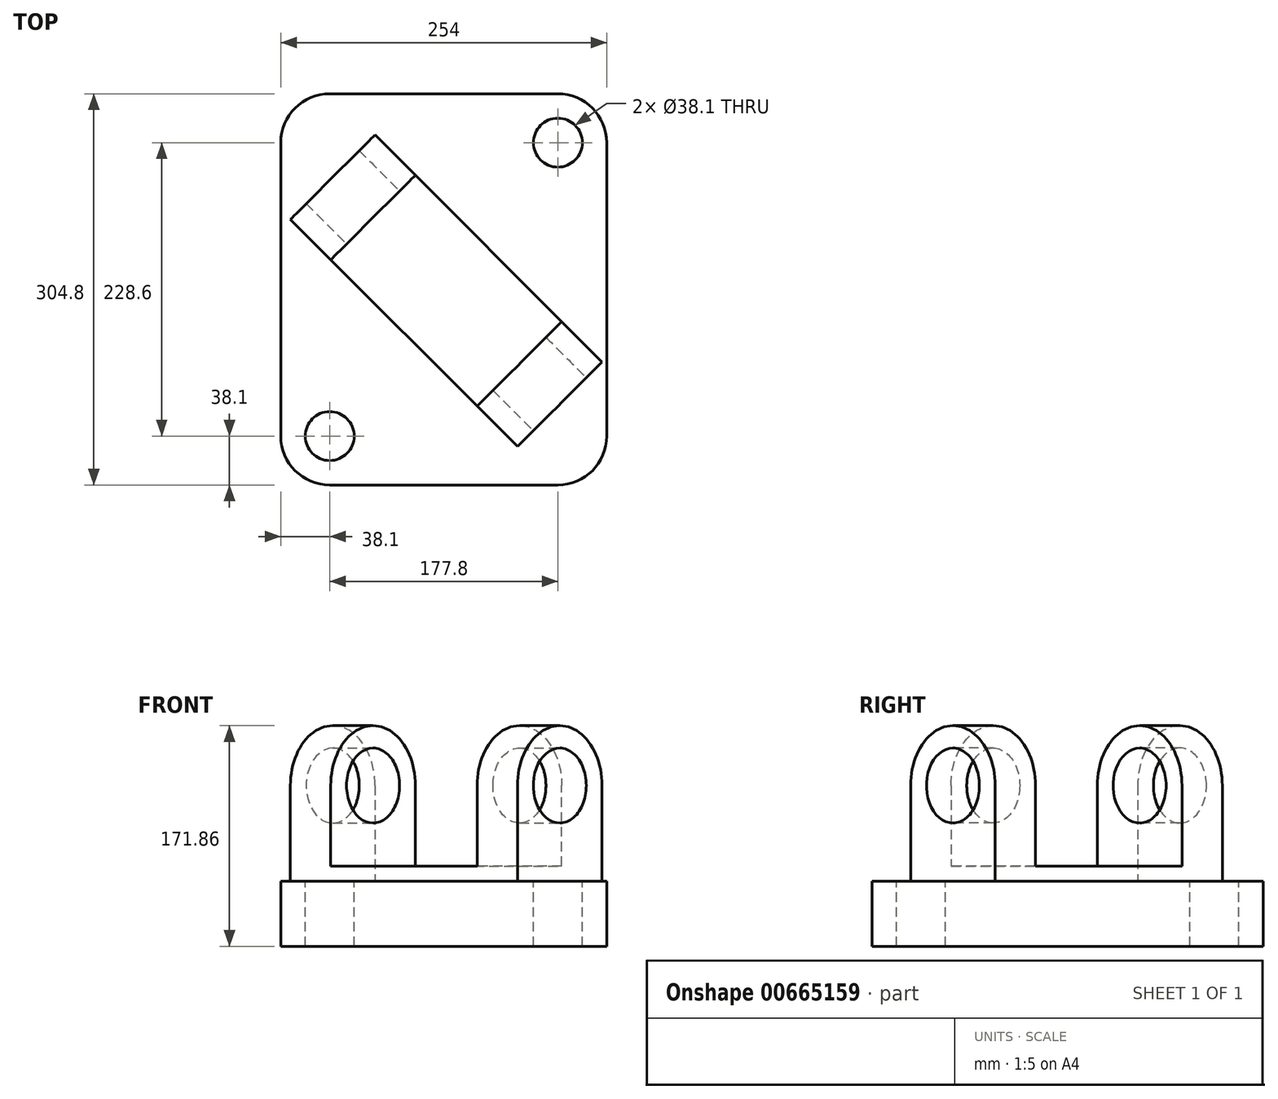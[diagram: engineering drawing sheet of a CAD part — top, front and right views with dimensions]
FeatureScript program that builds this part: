
annotation { "Feature Type Name" : "Feature", "Feature Type Description" : "" }
export const myFeature = defineFeature(function(context is Context, id is Id, definition is map)
    precondition{}
    {
        {
            var Q0;
            Q0=qCreatedBy(makeId("Top.planeOp"),FACE);
            var sketch = newSketch(context, id + "F0", { "sketchPlane" : qUnion([Q0])});
            skLineSegment(sketch, "E0", {"start": v(0, 0) * mm, "end": v(254, 0) * mm});
            skLineSegment(sketch, "E1", {"start": v(254, 0) * mm, "end": v(254, 304.8) * mm});
            skLineSegment(sketch, "E2", {"start": v(254, 304.8) * mm, "end": v(0, 304.8) * mm});
            skLineSegment(sketch, "E3", {"start": v(0, 304.8) * mm, "end": v(0, 0) * mm});
            skSolve(sketch);
        }
        {
            var Q0;
            Q0=makeQuery(id+"F0.imprint","IMPRINT",FACE,{"disambiguationData":[TD([[makeQuery(id+"F0.imprint","IMPRINT",EDGE,{"derivedFrom":sQuery(id+"F0.wireOp",EDGE,"E0")}),1.0]])]});
            extrude(context, id + "F1", {"entities" : qUnion([Q0]), "depth" : 50.8 * mm, "offsetDistance" : 25.4 * mm});
        }
        {
            var Q0;
            Q0=makeQuery(id+"F1.opExtrude","SWEPT_EDGE",EDGE,{"disambiguationData":[OSD([sQuery(id+"F0.wireOp",EDGE,"E2"),sQuery(id+"F0.wireOp",EDGE,"E3")])]});
            var Q1;
            Q1=makeQuery(id+"F1.opExtrude","SWEPT_EDGE",EDGE,{"disambiguationData":[OSD([sQuery(id+"F0.wireOp",EDGE,"E1"),sQuery(id+"F0.wireOp",EDGE,"E2")])]});
            var Q2;
            Q2=makeQuery(id+"F1.opExtrude","SWEPT_EDGE",EDGE,{"disambiguationData":[OSD([sQuery(id+"F0.wireOp",EDGE,"E0"),sQuery(id+"F0.wireOp",EDGE,"E1")])]});
            var Q3;
            Q3=makeQuery(id+"F1.opExtrude","SWEPT_EDGE",EDGE,{"disambiguationData":[OSD([sQuery(id+"F0.wireOp",EDGE,"E0"),sQuery(id+"F0.wireOp",EDGE,"E3")])]});
            fillet(context, id + "F2", {"entities" : qUnion([Q0, Q1, Q2, Q3]), "radius" : 38.1 * mm, "tangentPropagation" : true, "allowEdgeOverflow" : false});
        }
        {
            var Q0;
            Q0=makeQuery(id+"F1.opExtrude","CAP_FACE",FACE,{"disambiguationData":[OSD([sQuery(id+"F0.wireOp",EDGE,"E0"),sQuery(id+"F0.wireOp",EDGE,"E1"),sQuery(id+"F0.wireOp",EDGE,"E2"),sQuery(id+"F0.wireOp",EDGE,"E3")])],"isStart":false});
            var sketch = newSketch(context, id + "F3", { "sketchPlane" : qUnion([Q0])});
            skCircle(sketch, "E4", {"center": v(215.9, 266.7) * mm, "radius": 19.05 * mm});
            skCircle(sketch, "E5", {"center": v(38.1, 38.1) * mm, "radius": 19.05 * mm});
            skLineSegment(sketch, "E6", {"start": v(73.45, 272.84) * mm, "end": v(250.36, 95.93) * mm});
            skLineSegment(sketch, "E7", {"start": v(184.4, 29.97) * mm, "end": v(7.5, 206.88) * mm});
            skLineSegment(sketch, "E8", {"start": v(73.45, 272.84) * mm, "end": v(7.5, 206.88) * mm});
            skLineSegment(sketch, "E9", {"start": v(250.36, 95.93) * mm, "end": v(184.4, 29.97) * mm});
            skSolve(sketch);
        }
        {
            var Q0;
            Q0=makeQuery(id+"F3.imprint","IMPRINT",FACE,{"disambiguationData":[TD([[makeQuery(id+"F3.imprint","IMPRINT",EDGE,{"derivedFrom":sQuery(id+"F3.wireOp",EDGE,"E6")}),-1.0]])]});
            extrude(context, id + "F4", {"entities" : qUnion([Q0]), "operationType" : NewBodyOperationType.ADD, "depth" : 74.42 * mm, "offsetDistance" : 25.4 * mm});
        }
        {
            var Q0;
            Q0=makeQuery(id+"F4.opExtrude","SWEPT_FACE",FACE,{"disambiguationData":[OSD([sQuery(id+"F3.wireOp",EDGE,"E9")])]});
            var sketch = newSketch(context, id + "F5", { "sketchPlane" : qUnion([Q0])});
            skCircle(sketch, "E10", {"center": v(198.23, 125.22) * mm, "radius": 46.64 * mm});
            skCircle(sketch, "E11", {"center": v(198.23, 125.22) * mm, "radius": 29.21 * mm});
            skSolve(sketch);
        }
        {
            var Q0;
            {var subQ1=sQuery(id+"F3.wireOp",EDGE,"E9");var subQ2=makeQuery(id+"F4.opExtrude","CAP_EDGE",EDGE,{"disambiguationData":[OSD([subQ1])],"isStart":false});var subQ5=sQuery(id+"F5.wireOp",EDGE,"E11");var subQ6=makeQuery(id+"F5.imprint","INTERSECT",VERTEX,{"disambiguationData":[OD(0.0)],"derivedFrom":[subQ2,subQ5]});Q0=makeQuery(id+"F5.imprint","IMPRINT",FACE,{"disambiguationData":[TD([[makeQuery(id+"F5.imprint","IMPRINT",EDGE,{"disambiguationData":[TD([[subQ6,-1.0]])],"derivedFrom":subQ5}),-1.0]])]});}
            var Q1;
            {var subQ1=sQuery(id+"F3.wireOp",EDGE,"E9");var subQ2=makeQuery(id+"F4.opExtrude","CAP_EDGE",EDGE,{"disambiguationData":[OSD([subQ1])],"isStart":false});var subQ5=sQuery(id+"F5.wireOp",EDGE,"E11");var subQ6=makeQuery(id+"F5.imprint","INTERSECT",VERTEX,{"disambiguationData":[OD(0.0)],"derivedFrom":[subQ2,subQ5]});Q1=makeQuery(id+"F5.imprint","IMPRINT",FACE,{"disambiguationData":[TD([[makeQuery(id+"F5.imprint","IMPRINT",EDGE,{"disambiguationData":[TD([[subQ6,1.0]])],"derivedFrom":subQ5}),-1.0]])]});}
            extrude(context, id + "F6", {"entities" : qUnion([Q0, Q1]), "operationType" : NewBodyOperationType.ADD, "oppositeDirection" : true, "depth" : 250.2 * mm, "offsetDistance" : 25.4 * mm});
        }
        {
            var Q0;
            {var subQ0=sQuery(id+"F5.wireOp",EDGE,"E11");var subQ1=makeQuery(id+"F4.opExtrude","CAP_EDGE",EDGE,{"disambiguationData":[OSD([sQuery(id+"F3.wireOp",EDGE,"E9")])],"isStart":false});var subQ2=makeQuery(id+"F5.imprint","INTERSECT",VERTEX,{"disambiguationData":[OD(0.0)],"derivedFrom":[subQ1,subQ0]});Q0=makeQuery(id+"F5.imprint","IMPRINT",FACE,{"disambiguationData":[TD([[makeQuery(id+"F5.imprint","IMPRINT",EDGE,{"disambiguationData":[TD([[subQ2,1.0]])],"derivedFrom":subQ0}),1.0]])]});}
            extrude(context, id + "F7", {"entities" : qUnion([Q0]), "operationType" : NewBodyOperationType.REMOVE, "oppositeDirection" : true, "depth" : 250.2 * mm, "offsetDistance" : 25.4 * mm});
        }
        {
            var Q0;
            Q0=makeQuery(id+"F4.opExtrude","SWEPT_FACE",FACE,{"disambiguationData":[OSD([sQuery(id+"F3.wireOp",EDGE,"E7")])]});
            var sketch = newSketch(context, id + "F8", { "sketchPlane" : qUnion([Q0])});
            skLineSegment(sketch, "E12.0", {"start": v(64.75, 62.48) * mm, "end": v(-96.54, 62.48) * mm});
            skLineSegment(sketch, "E13.0", {"start": v(-96.54, 125.22) * mm, "end": v(-96.54, 62.48) * mm});
            skLineSegment(sketch, "E14.0", {"start": v(64.75, 125.22) * mm, "end": v(64.75, 62.48) * mm});
            skLineSegment(sketch, "E15", {"start": v(-96.54, 125.22) * mm, "end": v(-96.54, 180.46) * mm});
            skLineSegment(sketch, "E16", {"start": v(-96.54, 180.46) * mm, "end": v(64.75, 180.46) * mm});
            skLineSegment(sketch, "E17", {"start": v(64.75, 180.46) * mm, "end": v(64.75, 125.22) * mm});
            skSolve(sketch);
        }
        {
            var Q0;
            {var subQ0=sQuery(id+"F8.wireOp",EDGE,"E15");Q0=makeQuery(id+"F8.imprint","IMPRINT",FACE,{"disambiguationData":[TD([[makeQuery(id+"F8.imprint","IMPRINT",EDGE,{"derivedFrom":subQ0}),-1.0]])]});}
            var Q1;
            Q1=makeQuery(id+"F8.imprint","IMPRINT",FACE,{"disambiguationData":[TD([[makeQuery(id+"F8.imprint","IMPRINT",EDGE,{"derivedFrom":sQuery(id+"F8.wireOp",EDGE,"E12.0")}),-1.0]])]});
            extrude(context, id + "F9", {"entities" : qUnion([Q0, Q1]), "operationType" : NewBodyOperationType.REMOVE, "oppositeDirection" : true, "depth" : 93.3 * mm, "offsetDistance" : 25.4 * mm});
        }
        {
            var Q0;
            Q0=makeQuery(id+"F3.imprint","IMPRINT",FACE,{"disambiguationData":[TD([[makeQuery(id+"F3.imprint","IMPRINT",EDGE,{"derivedFrom":sQuery(id+"F3.wireOp",EDGE,"E4")}),1.0]])]});
            var Q1;
            Q1=makeQuery(id+"F3.imprint","IMPRINT",FACE,{"disambiguationData":[TD([[makeQuery(id+"F3.imprint","IMPRINT",EDGE,{"derivedFrom":sQuery(id+"F3.wireOp",EDGE,"E5")}),1.0]])]});
            extrude(context, id + "F10", {"entities" : qUnion([Q0, Q1]), "operationType" : NewBodyOperationType.REMOVE, "oppositeDirection" : true, "depth" : 50.8 * mm, "offsetDistance" : 25.4 * mm});
        }
    });
